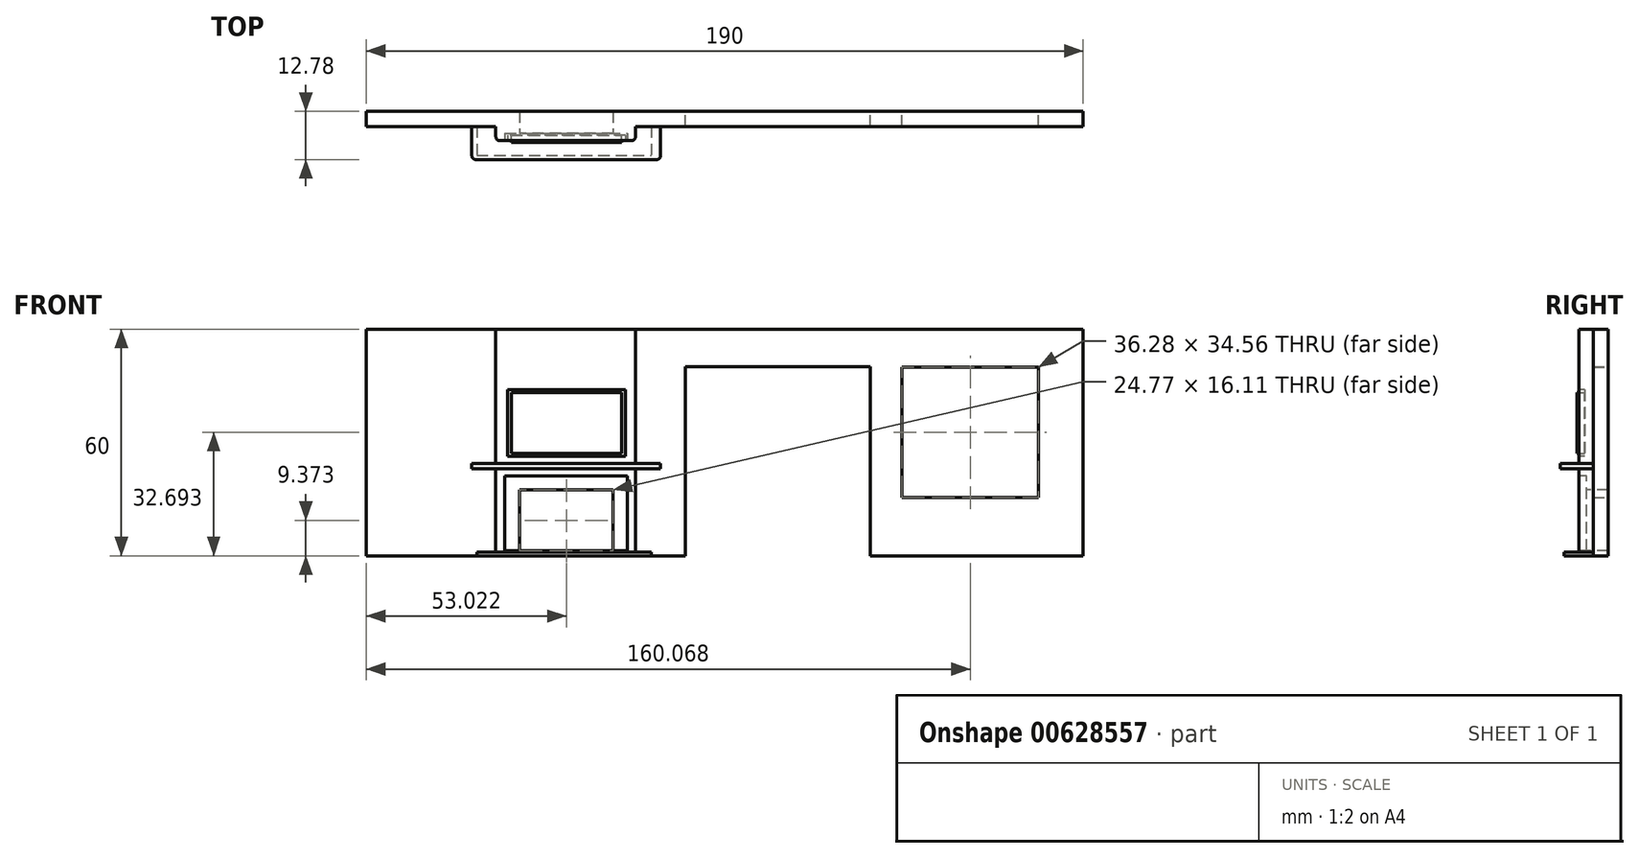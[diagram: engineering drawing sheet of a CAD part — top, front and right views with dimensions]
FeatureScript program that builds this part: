
annotation { "Feature Type Name" : "Feature", "Feature Type Description" : "" }
export const myFeature = defineFeature(function(context is Context, id is Id, definition is map)
    precondition{}
    {
        {
            var Q0;
            Q0=qCreatedBy(makeId("Front.planeOp"),FACE);
            var sketch = newSketch(context, id + "F0", { "sketchPlane" : qUnion([Q0])});
            skLineSegment(sketch, "E0.bottom", {"start": v(-94.15, 30.56) * mm, "end": v(95.85, 30.56) * mm});
            skLineSegment(sketch, "E0.top", {"start": v(-94.15, -29.44) * mm, "end": v(-9.58, -29.44) * mm});
            skLineSegment(sketch, "E0.left", {"start": v(-94.15, 30.56) * mm, "end": v(-94.15, -29.44) * mm});
            skLineSegment(sketch, "E0.right", {"start": v(95.85, 30.56) * mm, "end": v(95.85, -29.44) * mm});
            skLineSegment(sketch, "E1.top", {"start": v(39.4, 20.67) * mm, "end": v(-9.58, 20.67) * mm});
            skLineSegment(sketch, "E1.left", {"start": v(39.4, -29.44) * mm, "end": v(39.4, 20.67) * mm});
            skLineSegment(sketch, "E1.right", {"start": v(-9.58, -29.44) * mm, "end": v(-9.58, 20.67) * mm});
            skLineSegment(sketch, "E2.bottom", {"start": v(47.78, -14.03) * mm, "end": v(84.06, -14.03) * mm});
            skLineSegment(sketch, "E2.top", {"start": v(47.78, 20.53) * mm, "end": v(84.06, 20.53) * mm});
            skLineSegment(sketch, "E2.left", {"start": v(47.78, -14.03) * mm, "end": v(47.78, 20.53) * mm});
            skLineSegment(sketch, "E2.right", {"start": v(84.06, -14.03) * mm, "end": v(84.06, 20.53) * mm});
            skLineSegment(sketch, "E3.trimOffspring", {"start": v(39.4, -29.44) * mm, "end": v(95.85, -29.44) * mm});
            skSolve(sketch);
        }
        {
            var Q0;
            Q0=makeQuery(id+"F0.imprint","IMPRINT",FACE,{"disambiguationData":[TD([[makeQuery(id+"F0.imprint","IMPRINT",EDGE,{"derivedFrom":sQuery(id+"F0.wireOp",EDGE,"E0.bottom")}),-1.0]])]});
            extrude(context, id + "F1", {"entities" : qUnion([Q0]), "depth" : 4 * mm, "offsetDistance" : 25 * mm});
        }
        {
            var Q0;
            Q0=makeQuery(id+"F1.opExtrude","SWEPT_FACE",FACE,{"disambiguationData":[OSD([sQuery(id+"F0.wireOp",EDGE,"E0.top")])]});
            var sketch = newSketch(context, id + "F2", { "sketchPlane" : qUnion([Q0])});
            skLineSegment(sketch, "E4.bottom", {"start": v(-59.83, 0) * mm, "end": v(-22.85, 0) * mm});
            skLineSegment(sketch, "E4.top", {"start": v(-58.83, 7.78) * mm, "end": v(-23.85, 7.78) * mm});
            skLineSegment(sketch, "E4.left", {"start": v(-59.83, 0) * mm, "end": v(-59.83, 6.78) * mm});
            skLineSegment(sketch, "E4.right", {"start": v(-22.85, 0) * mm, "end": v(-22.85, 6.78) * mm});
            skPoint(sketch, "E5.visualSharp", {"position": v(-22.85, 7.78) * mm});
            skArc(sketch, "E5.filletArc", {"start": v(-22.85, 6.78) * mm, "mid": v(-23.14, 7.49) * mm, "end": v(-23.85, 7.78) * mm});
            skPoint(sketch, "E6.visualSharp", {"position": v(-59.83, 7.78) * mm});
            skArc(sketch, "E6.filletArc", {"start": v(-58.83, 7.78) * mm, "mid": v(-59.53, 7.49) * mm, "end": v(-59.83, 6.78) * mm});
            skSolve(sketch);
        }
        {
            var Q0;
            Q0=makeQuery(id+"F2.imprint","IMPRINT",FACE,{"disambiguationData":[TD([[makeQuery(id+"F2.imprint","IMPRINT",EDGE,{"derivedFrom":sQuery(id+"F2.wireOp",EDGE,"E4.top")}),-1.0]])]});
            extrude(context, id + "F3", {"entities" : qUnion([Q0]), "operationType" : NewBodyOperationType.ADD, "oppositeDirection" : true, "depth" : 60 * mm, "offsetDistance" : 25 * mm});
        }
        {
            var Q0;
            Q0=makeQuery(id+"F0.imprint","IMPRINT",FACE,{"disambiguationData":[TD([[makeQuery(id+"F0.imprint","IMPRINT",EDGE,{"derivedFrom":sQuery(id+"F0.wireOp",EDGE,"E0.bottom")}),-1.0]])]});
            var sketch = newSketch(context, id + "F4", { "sketchPlane" : qUnion([Q0])});
            skLineSegment(sketch, "E7.bottom", {"start": v(-28.74, -28.12) * mm, "end": v(-53.51, -28.12) * mm});
            skLineSegment(sketch, "E7.top", {"start": v(-28.74, -12.01) * mm, "end": v(-53.51, -12.01) * mm});
            skLineSegment(sketch, "E7.left", {"start": v(-28.74, -28.12) * mm, "end": v(-28.74, -12.01) * mm});
            skLineSegment(sketch, "E7.right", {"start": v(-53.51, -28.12) * mm, "end": v(-53.51, -12.01) * mm});
            skSolve(sketch);
        }
        {
            var Q0;
            Q0 = qSketchRegion(id + "F4", true);
            extrude(context, id + "F5", {"entities" : qUnion([Q0]), "operationType" : NewBodyOperationType.ADD, "depth" : 25 * mm, "offsetDistance" : 25 * mm});
        }
        {
            var Q0;
            Q0=makeQuery(id+"F5.opExtrude","CAP_FACE",FACE,{"disambiguationData":[OSD([sQuery(id+"F4.wireOp",EDGE,"E7.bottom"),sQuery(id+"F4.wireOp",EDGE,"E7.top"),sQuery(id+"F4.wireOp",EDGE,"E7.left"),sQuery(id+"F4.wireOp",EDGE,"E7.right")])],"isStart":false});
            extrude(context, id + "F6", {"entities" : qUnion([Q0]), "operationType" : NewBodyOperationType.REMOVE, "oppositeDirection" : true, "depth" : 28.22 * mm, "offsetDistance" : 25 * mm});
        }
        {
            var Q0;
            Q0=makeQuery(id+"F3.opExtrude","SWEPT_FACE",FACE,{"disambiguationData":[OSD([sQuery(id+"F2.wireOp",EDGE,"E4.top")])]});
            var sketch = newSketch(context, id + "F7", { "sketchPlane" : qUnion([Q0])});
            skLineSegment(sketch, "E8.bottom", {"start": v(-57.42, -28.13) * mm, "end": v(-24.93, -28.13) * mm});
            skLineSegment(sketch, "E8.top", {"start": v(-57.42, -8.29) * mm, "end": v(-24.93, -8.29) * mm});
            skLineSegment(sketch, "E8.left", {"start": v(-57.42, -28.13) * mm, "end": v(-57.42, -8.29) * mm});
            skLineSegment(sketch, "E8.right", {"start": v(-24.93, -28.13) * mm, "end": v(-24.93, -8.29) * mm});
            skSolve(sketch);
        }
        {
            var Q0;
            Q0=makeQuery(id+"F7.imprint","IMPRINT",FACE,{"disambiguationData":[TD([[makeQuery(id+"F7.imprint","IMPRINT",EDGE,{"derivedFrom":sQuery(id+"F7.wireOp",EDGE,"E8.bottom")}),1.0]])]});
            extrude(context, id + "F8", {"entities" : qUnion([Q0]), "operationType" : NewBodyOperationType.REMOVE, "oppositeDirection" : true, "depth" : 1.98 * mm, "offsetDistance" : 25 * mm});
        }
        {
            var Q0;
            {var subQ0=sQuery(id+"F2.wireOp",EDGE,"E4.bottom");Q0=makeQuery(id+"F2.imprint","IMPRINT",FACE,{"disambiguationData":[TD([[makeQuery(id+"F2.imprint","IMPRINT",EDGE,{"derivedFrom":subQ0}),1.0]])]});}
            var sketch = newSketch(context, id + "F9", { "sketchPlane" : qUnion([Q0])});
            skLineSegment(sketch, "E9.bottom", {"start": v(-64.86, 0) * mm, "end": v(-18.6, 0) * mm});
            skLineSegment(sketch, "E9.top", {"start": v(-64.86, 11.7) * mm, "end": v(-18.6, 11.7) * mm});
            skLineSegment(sketch, "E9.left", {"start": v(-64.86, 0) * mm, "end": v(-64.86, 11.7) * mm});
            skLineSegment(sketch, "E9.right", {"start": v(-18.6, 0) * mm, "end": v(-18.6, 11.7) * mm});
            skSolve(sketch);
        }
        {
            var Q0;
            Q0=makeQuery(id+"F9.imprint","IMPRINT",FACE,{"disambiguationData":[TD([[makeQuery(id+"F9.imprint","IMPRINT",EDGE,{"derivedFrom":sQuery(id+"F9.wireOp",EDGE,"E9.top")}),-1.0]])]});
            var Q1;
            {var subQ1=sQuery(id+"F2.wireOp",EDGE,"E4.left");var subQ3=sQuery(id+"F0.wireOp",EDGE,"E0.top");var subQ5=makeQuery(id+"F1.opExtrude","CAP_EDGE",EDGE,{"disambiguationData":[OSD([subQ3])],"isStart":false});var subQ6=makeQuery(id+"F2.imprint","INTERSECT",VERTEX,{"derivedFrom":[subQ5,subQ1]});Q1=makeQuery(id+"F9.imprint","IMPRINT",FACE,{"disambiguationData":[TD([[makeQuery(id+"F9.imprint","IMPRINT",EDGE,{"derivedFrom":makeQuery(id+"F2.imprint","IMPRINT",EDGE,{"disambiguationData":[TD([[subQ6,-1.0]])],"derivedFrom":subQ5})}),-1.0]])]});}
            extrude(context, id + "F10", {"entities" : qUnion([Q0, Q1]), "operationType" : NewBodyOperationType.ADD, "oppositeDirection" : true, "depth" : 0.94 * mm, "offsetDistance" : 25 * mm});
        }
        {
            var Q0;
            Q0=makeQuery(id+"F3.opExtrude","SWEPT_FACE",FACE,{"disambiguationData":[OSD([sQuery(id+"F2.wireOp",EDGE,"E4.top")])]});
            var sketch = newSketch(context, id + "F11", { "sketchPlane" : qUnion([Q0])});
            skLineSegment(sketch, "E10.bottom", {"start": v(-55.73, -2.32) * mm, "end": v(-26.5, -2.32) * mm});
            skLineSegment(sketch, "E10.top", {"start": v(-55.73, 13.83) * mm, "end": v(-26.5, 13.83) * mm});
            skLineSegment(sketch, "E10.left", {"start": v(-55.73, -2.32) * mm, "end": v(-55.73, 13.83) * mm});
            skLineSegment(sketch, "E10.right", {"start": v(-26.5, -2.32) * mm, "end": v(-26.5, 13.83) * mm});
            skSolve(sketch);
        }
        {
            var Q0;
            Q0=makeQuery(id+"F11.imprint","IMPRINT",FACE,{"disambiguationData":[TD([[makeQuery(id+"F11.imprint","IMPRINT",EDGE,{"derivedFrom":sQuery(id+"F11.wireOp",EDGE,"E10.bottom")}),1.0]])]});
            extrude(context, id + "F12", {"entities" : qUnion([Q0]), "operationType" : NewBodyOperationType.ADD, "depth" : .5 * mm, "offsetDistance" : 25 * mm});
        }
        {
            var Q0;
            Q0=makeQuery(id+"F3.opExtrude","SWEPT_FACE",FACE,{"disambiguationData":[OSD([sQuery(id+"F2.wireOp",EDGE,"E4.top")])]});
            var sketch = newSketch(context, id + "F13", { "sketchPlane" : qUnion([Q0])});
            skLineSegment(sketch, "E11.bottom", {"start": v(-25.5, 14.56) * mm, "end": v(-56.73, 14.56) * mm});
            skLineSegment(sketch, "E11.top", {"start": v(-25.5, -3.05) * mm, "end": v(-56.73, -3.05) * mm});
            skLineSegment(sketch, "E11.left", {"start": v(-25.5, 14.56) * mm, "end": v(-25.5, -3.05) * mm});
            skLineSegment(sketch, "E11.right", {"start": v(-56.73, 14.56) * mm, "end": v(-56.73, -3.05) * mm});
            skPoint(sketch, "E11.middle", {"position": v(-41.12, 5.76) * mm});
            skPoint(sketch, "E11.middle.positionSnap0", {"position": v(-55.73, 5.76) * mm});
            skPoint(sketch, "E11.middle.positionSnap1", {"position": v(-41.12, -2.32) * mm});
            skPoint(sketch, "E11.centerSnap0", {"position": v(-55.73, 5.76) * mm});
            skPoint(sketch, "E11.centerSnap1", {"position": v(-41.12, -2.32) * mm});
            skSolve(sketch);
        }
        {
            var Q0;
            Q0=makeQuery(id+"F13.imprint","IMPRINT",FACE,{"disambiguationData":[TD([[makeQuery(id+"F13.imprint","IMPRINT",EDGE,{"derivedFrom":sQuery(id+"F13.wireOp",EDGE,"E11.bottom")}),1.0]])]});
            extrude(context, id + "F14", {"entities" : qUnion([Q0]), "operationType" : NewBodyOperationType.REMOVE, "oppositeDirection" : true, "depth" : 1.5 * mm, "offsetDistance" : 25 * mm});
        }
        {
            var Q0;
            Q0=makeQuery(id+"F3.opExtrude","SWEPT_FACE",FACE,{"disambiguationData":[OSD([sQuery(id+"F2.wireOp",EDGE,"E4.top")])]});
            var sketch = newSketch(context, id + "F15", { "sketchPlane" : qUnion([Q0])});
            skLineSegment(sketch, "E12.bottom", {"start": v(-16.17, -6.36) * mm, "end": v(-66.17, -6.36) * mm});
            skLineSegment(sketch, "E12.top", {"start": v(-16.17, -4.94) * mm, "end": v(-66.17, -4.94) * mm});
            skLineSegment(sketch, "E12.left", {"start": v(-16.17, -6.36) * mm, "end": v(-16.17, -4.94) * mm});
            skLineSegment(sketch, "E12.right", {"start": v(-66.17, -6.36) * mm, "end": v(-66.17, -4.94) * mm});
            skPoint(sketch, "E12.middle", {"position": v(-41.17, -5.65) * mm});
            skPoint(sketch, "E12.middle.positionSnap0", {"position": v(-41.17, -8.29) * mm});
            skPoint(sketch, "E12.centerSnap0", {"position": v(-41.17, -8.29) * mm});
            skSolve(sketch);
        }
        {
            var Q0;
            Q0=makeQuery(id+"F15.imprint","IMPRINT",FACE,{"disambiguationData":[TD([[makeQuery(id+"F15.imprint","IMPRINT",EDGE,{"derivedFrom":sQuery(id+"F15.wireOp",EDGE,"E12.bottom")}),-1.0]])]});
            extrude(context, id + "F16", {"entities" : qUnion([Q0]), "operationType" : NewBodyOperationType.ADD, "depth" : 5 * mm, "offsetDistance" : 25 * mm, "hasSecondDirection" : true, "secondDirectionOppositeDirection" : true, "secondDirectionDepth" : 4.83 * mm});
        }
        {
            var Q0;
            Q0=makeQuery(id+"F16.opExtrude","CAP_EDGE",EDGE,{"disambiguationData":[OSD([sQuery(id+"F15.wireOp",EDGE,"E12.left")])],"isStart":false});
            var Q1;
            Q1=makeQuery(id+"F16.opExtrude","CAP_EDGE",EDGE,{"disambiguationData":[OSD([sQuery(id+"F15.wireOp",EDGE,"E12.right")])],"isStart":false});
            fillet(context, id + "F17", {"entities" : qUnion([Q0, Q1]), "radius" : 1 * mm, "tangentPropagation" : true, "allowEdgeOverflow" : false});
        }
    });
